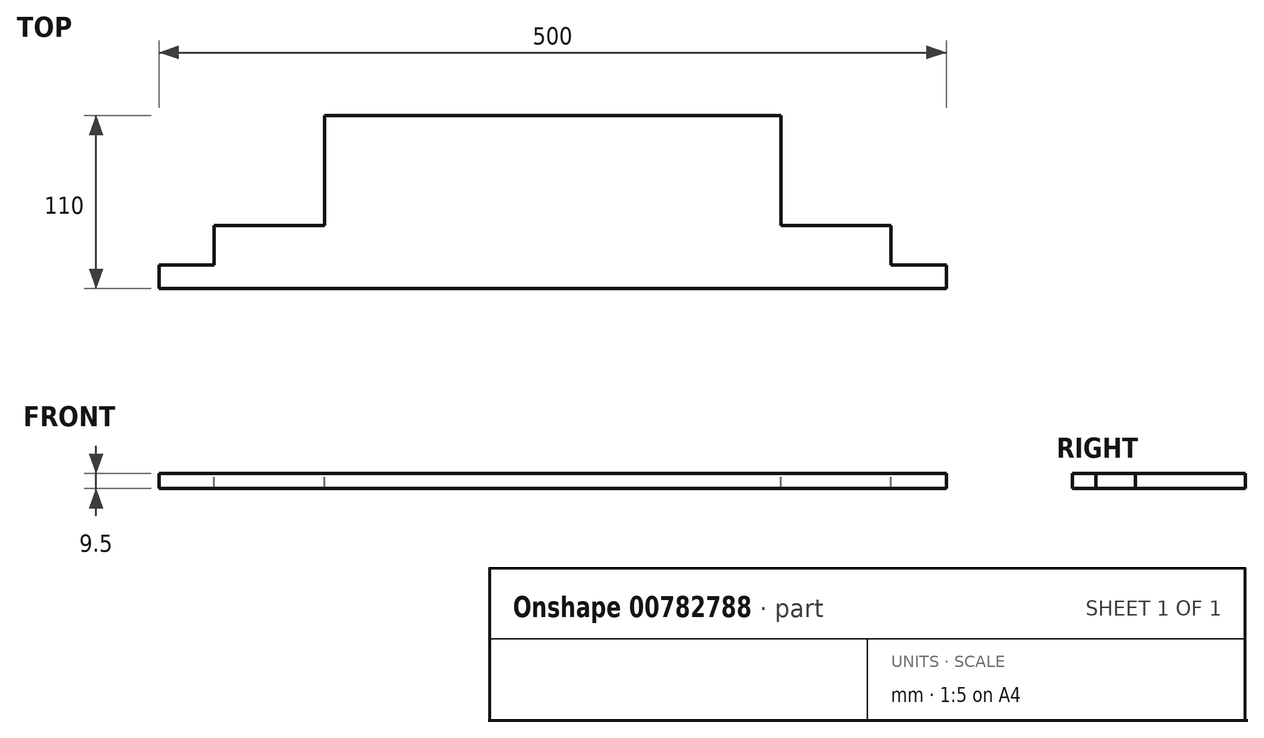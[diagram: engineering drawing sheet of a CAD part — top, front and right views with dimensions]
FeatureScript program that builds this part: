
annotation { "Feature Type Name" : "Feature", "Feature Type Description" : "" }
export const myFeature = defineFeature(function(context is Context, id is Id, definition is map)
    precondition{}
    {
        {
            var Q0;
            Q0=qCreatedBy(makeId("Top.planeOp"),FACE);
            var sketch = newSketch(context, id + "F0", { "sketchPlane" : qUnion([Q0])});
            skLineSegment(sketch, "E0.bottom", {"start": v(-32.05, -21.52) * mm, "end": v(467.95, -21.52) * mm});
            skLineSegment(sketch, "E0.top", {"start": v(-32.05, 88.48) * mm, "end": v(467.95, 88.48) * mm});
            skLineSegment(sketch, "E0.left", {"start": v(-32.05, -21.52) * mm, "end": v(-32.05, 88.48) * mm});
            skLineSegment(sketch, "E0.right", {"start": v(467.95, -21.52) * mm, "end": v(467.95, 88.48) * mm});
            skLineSegment(sketch, "E1", {"start": v(467.95, 88.48) * mm, "end": v(432.95, 88.48) * mm});
            skLineSegment(sketch, "E2", {"start": v(432.95, 88.48) * mm, "end": v(432.95, -21.52) * mm});
            skLineSegment(sketch, "E3", {"start": v(432.95, -21.52) * mm, "end": v(432.95, 18.48) * mm});
            skLineSegment(sketch, "E4", {"start": v(-32.05, 88.48) * mm, "end": v(2.95, 88.48) * mm});
            skLineSegment(sketch, "E5", {"start": v(2.95, 88.48) * mm, "end": v(2.95, -21.52) * mm});
            skLineSegment(sketch, "E6", {"start": v(432.95, 18.48) * mm, "end": v(362.95, 18.48) * mm});
            skLineSegment(sketch, "E7", {"start": v(362.95, 18.48) * mm, "end": v(362.95, 88.48) * mm});
            skLineSegment(sketch, "E8", {"start": v(2.95, 88.48) * mm, "end": v(2.95, 18.48) * mm});
            skLineSegment(sketch, "E9", {"start": v(2.95, 18.48) * mm, "end": v(72.95, 18.48) * mm});
            skLineSegment(sketch, "E10", {"start": v(72.95, 18.48) * mm, "end": v(72.95, 88.48) * mm});
            skLineSegment(sketch, "E11.0", {"start": v(-32.05, -6.52) * mm, "end": v(467.95, -6.52) * mm});
            skSolve(sketch);
        }
        {
            var Q0;
            {var subQ4=sQuery(id+"F0.wireOp",EDGE,"E4");Q0=makeQuery(id+"F0.imprint","IMPRINT",FACE,{"disambiguationData":[TD([[makeQuery(id+"F0.imprint","IMPRINT",EDGE,{"derivedFrom":subQ4}),-1.0]])]});}
            var Q1;
            {var subQ0=sQuery(id+"F0.wireOp",EDGE,"E6");Q1=makeQuery(id+"F0.imprint","IMPRINT",FACE,{"disambiguationData":[TD([[makeQuery(id+"F0.imprint","IMPRINT",EDGE,{"derivedFrom":subQ0}),1.0]])]});}
            var Q2;
            {var subQ6=sQuery(id+"F0.wireOp",EDGE,"E1");Q2=makeQuery(id+"F0.imprint","IMPRINT",FACE,{"disambiguationData":[TD([[makeQuery(id+"F0.imprint","IMPRINT",EDGE,{"derivedFrom":subQ6}),1.0]])]});}
            var Q3;
            {var subQ0=sQuery(id+"F0.wireOp",EDGE,"E0.left");var subQ1=sQuery(id+"F0.wireOp",EDGE,"E0.bottom");var subQ2=makeQuery(id+"F0.imprint","INTERSECT",VERTEX,{"derivedFrom":[subQ1,subQ0]});Q3=makeQuery(id+"F0.imprint","IMPRINT",FACE,{"disambiguationData":[TD([[makeQuery(id+"F0.imprint","IMPRINT",EDGE,{"disambiguationData":[TD([[subQ2,-1.0]])],"derivedFrom":subQ1}),1.0]])]});}
            var Q4;
            {var subQ0=sQuery(id+"F0.wireOp",EDGE,"E3");var subQ1=sQuery(id+"F0.wireOp",EDGE,"E0.bottom");var subQ2=makeQuery(id+"F0.imprint","INTERSECT",VERTEX,{"derivedFrom":[subQ1,subQ0]});Q4=makeQuery(id+"F0.imprint","IMPRINT",FACE,{"disambiguationData":[TD([[makeQuery(id+"F0.imprint","IMPRINT",EDGE,{"disambiguationData":[TD([[subQ2,1.0]])],"derivedFrom":subQ1}),1.0]])]});}
            var Q5;
            {var subQ0=sQuery(id+"F0.wireOp",EDGE,"E0.right");var subQ1=sQuery(id+"F0.wireOp",EDGE,"E0.bottom");var subQ2=makeQuery(id+"F0.imprint","INTERSECT",VERTEX,{"derivedFrom":[subQ1,subQ0]});Q5=makeQuery(id+"F0.imprint","IMPRINT",FACE,{"disambiguationData":[TD([[makeQuery(id+"F0.imprint","IMPRINT",EDGE,{"disambiguationData":[TD([[subQ2,1.0]])],"derivedFrom":subQ1}),1.0]])]});}
            extrude(context, id + "F1", {"entities" : qUnion([Q0, Q1, Q2, Q3, Q4, Q5]), "oppositeDirection" : true, "depth" : 9.5 * mm, "offsetDistance" : 25 * mm});
        }
        {
            var Q0;
            Q0=makeQuery(id+"F1.opExtrude","CAP_FACE",FACE,{"disambiguationData":[OSD([sQuery(id+"F0.wireOp",EDGE,"E0.bottom"),sQuery(id+"F0.wireOp",EDGE,"E0.top"),sQuery(id+"F0.wireOp",EDGE,"E0.left"),sQuery(id+"F0.wireOp",EDGE,"E0.right"),sQuery(id+"F0.wireOp",EDGE,"E1"),sQuery(id+"F0.wireOp",EDGE,"E2"),sQuery(id+"F0.wireOp",EDGE,"E4"),sQuery(id+"F0.wireOp",EDGE,"E6"),sQuery(id+"F0.wireOp",EDGE,"E7"),sQuery(id+"F0.wireOp",EDGE,"E8"),sQuery(id+"F0.wireOp",EDGE,"E9"),sQuery(id+"F0.wireOp",EDGE,"E10")])],"isStart":true});
            var sketch = newSketch(context, id + "F2", { "sketchPlane" : qUnion([Q0])});
            skLineSegment(sketch, "E12", {"start": v(2.95, 18.48) * mm, "end": v(2.95, 23.48) * mm});
            skLineSegment(sketch, "E13", {"start": v(2.95, 23.48) * mm, "end": v(72.95, 23.48) * mm});
            skLineSegment(sketch, "E14", {"start": v(72.95, 23.48) * mm, "end": v(72.95, 18.48) * mm});
            skLineSegment(sketch, "E15", {"start": v(362.95, 18.48) * mm, "end": v(362.95, 23.48) * mm});
            skLineSegment(sketch, "E16", {"start": v(362.95, 23.48) * mm, "end": v(432.95, 23.48) * mm});
            skLineSegment(sketch, "E17", {"start": v(432.95, 23.48) * mm, "end": v(432.95, 18.48) * mm});
            skSolve(sketch);
        }
    });
